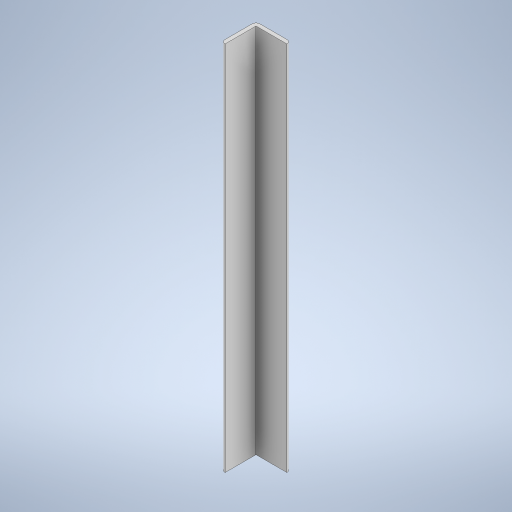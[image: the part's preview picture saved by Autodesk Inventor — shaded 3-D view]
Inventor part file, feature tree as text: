
AUTODESK INVENTOR PART (.ipt)
format: ipt  version: 2024.2 (Build 282272000, 272)  size: 240,640 bytes
history: native  units: in
note: dims shown in document units (in); Inventor stores cm internally (conversion verified against a paired STEP export)
features: extrude x1, fillet x1, sketch x1
ambient origin geometry x8: Origin, YZ Plane, XZ Plane, XY Plane, X Axis, Y Axis, Z Axis, Center Point
bodies: Solid1 (feature_tree)
feature tree (3):
  extrude  "Extrusion1"  Depth=0.125in
  fillet  "Fillet1"  Radius=1.125in
  sketch  "Sketch1"  dims[d0=0.125in d1=0.125in d2=1.125in d3=1.125in d4=12.0in d5=0.0in d6=0.125in]
